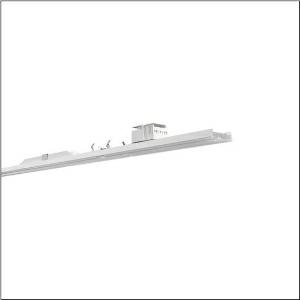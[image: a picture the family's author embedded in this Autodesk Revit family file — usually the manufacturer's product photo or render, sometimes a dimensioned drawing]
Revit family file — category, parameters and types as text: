
# Revit family: licross_r__11_recessed_ho_51tl11dv4m1r_4563
name_source: partatom
category: Lighting Fixtures
units: mm (PartAtom-declared; Revit-internal decimal feet)

## family parameters
Cut with Voids When Loaded = No
Host = Face
Light Source = No
Part Type = Normal
Room Calculation Point = No
Round Connector Dimension = Use Diameter
Shared = No

## types (1)
- --- (1 x LED, 26170 lm, 150.2 W, 4000K)
    Apparent Load = 150 VA
    CIE Flux Codes = 87 95 99 100 100
    Color Rendering = 80
    Color Temperature = 4000K
    Default Elevation = 1800 mm
    Description = Licross® 11 Recessed HOluminaire insert, length: 2.250mm, width: 66mm, height: 67mm, LED rated luminous flux: 26.170lm, light colour: 840, control gear: DALI 2, control gear: ECG DALI, with plug, 5-pole, with phase selection, mains connection: 220..240V, AC, 50/60Hz, halogen-free wiring, primary optical cover: cover, of PMMA, light emission: direct distribution, protection rating (complete): IP40, insulation class (complete): insulation class I (protective earthing), certification: CE, ENEC, VDE, protection symbol: D if used in an environment without relevant dust loads with corresponding accessories, permissible ambient temperature for indoor applications: -35..+35°C, corresponds to IFS (International Featured Standards) requirements for safety and quality in the food industry, reducing of maximum allowable ambient temperature of 5°C with ceiling mounting, packaging unit: 1 piece
    Height = 58 mm
    Lamp = 1 x LED
    Lamp Light Flux = 26170 lm
    Lamp Power = 150.2 W
    Lamp count = 1
    Length = 2250 mm
    Luminous efficacy = 174 lm/W
    Manufacturer = Siteco
    ModVariant = No
    Model = 51TL11DV4M1R
    Mounting Place = Ceiling
    Mounting Type = Pendant
    Number of Poles = 1
    OnlyDefault = Yes
    Power Factor = 1
    Product Name = Licross® 11 Recessed HO
    Product group = luminaire insert
    ProductGroupID = 902
    Protection Class = Protection class I
    Protection Degree = IP 40
    RLX_Detail_Level = 1
    RlxData = <blob elided: 27149 chars, md5=f20ce8f5>
    Socket = socket
    Standby Power = 0 W
    System Light Flux = 26169 lm
    System Power = 150 W
    Type Comments = factory setting: luminous flux: 100 % | dim-lin: 254 | 575 mA
    Type Image = l_1266722.jpg
    URL = http://relux.com
    VarID = @adj_133036
    Voltage = 0 V
    Weight = 0.00 kg
    Width = 66 mm

## geometry (parser evidence)
native form markers: Blend x4, Sweep x12
no freeform markers — native parametric forms only
